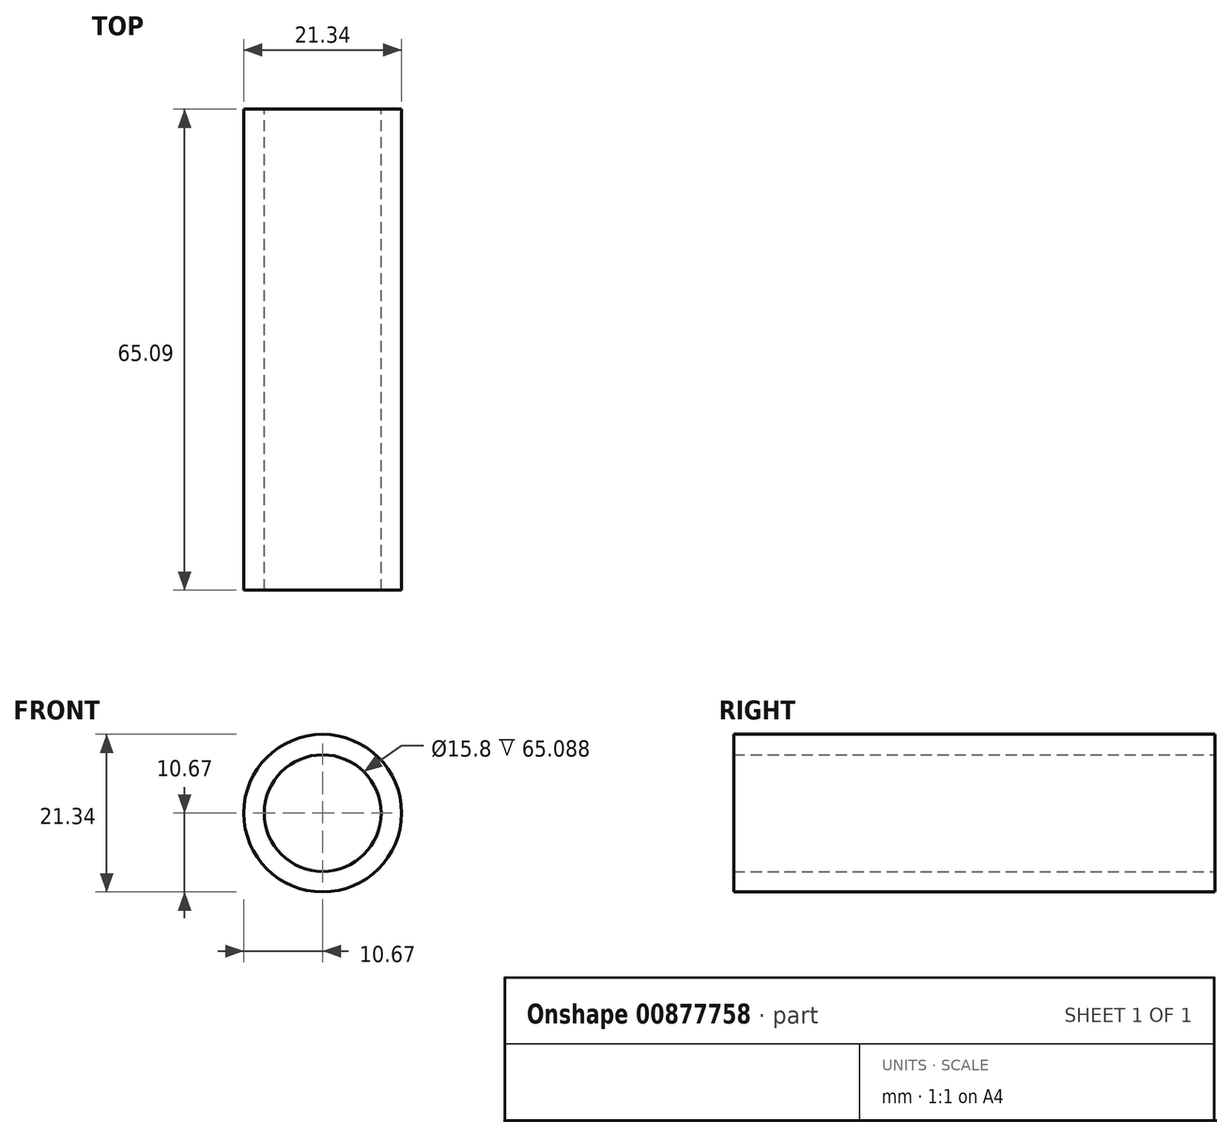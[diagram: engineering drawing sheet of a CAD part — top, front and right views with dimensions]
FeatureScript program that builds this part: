
annotation { "Feature Type Name" : "Feature", "Feature Type Description" : "" }
export const myFeature = defineFeature(function(context is Context, id is Id, definition is map)
    precondition{}
    {
        {
            var Q0;
            Q0=qCreatedBy(makeId("Front.planeOp"),FACE);
            var sketch = newSketch(context, id + "F0", { "sketchPlane" : qUnion([Q0])});
            skCircle(sketch, "E0", {"center": v(0, 0) * mm, "radius": 10.67 * mm});
            skCircle(sketch, "E1", {"center": v(0, 0) * mm, "radius": 7.9 * mm});
            skSolve(sketch);
        }
        {
            var Q0;
            Q0=makeQuery(id+"F0.imprint","IMPRINT",FACE,{"disambiguationData":[TD([[makeQuery(id+"F0.imprint","IMPRINT",EDGE,{"derivedFrom":sQuery(id+"F0.wireOp",EDGE,"E0")}),1.0]])]});
            extrude(context, id + "F1", {"entities" : qUnion([Q0]), "depth" : 65.1 * mm, "offsetDistance" : 25.4 * mm});
        }
    });
